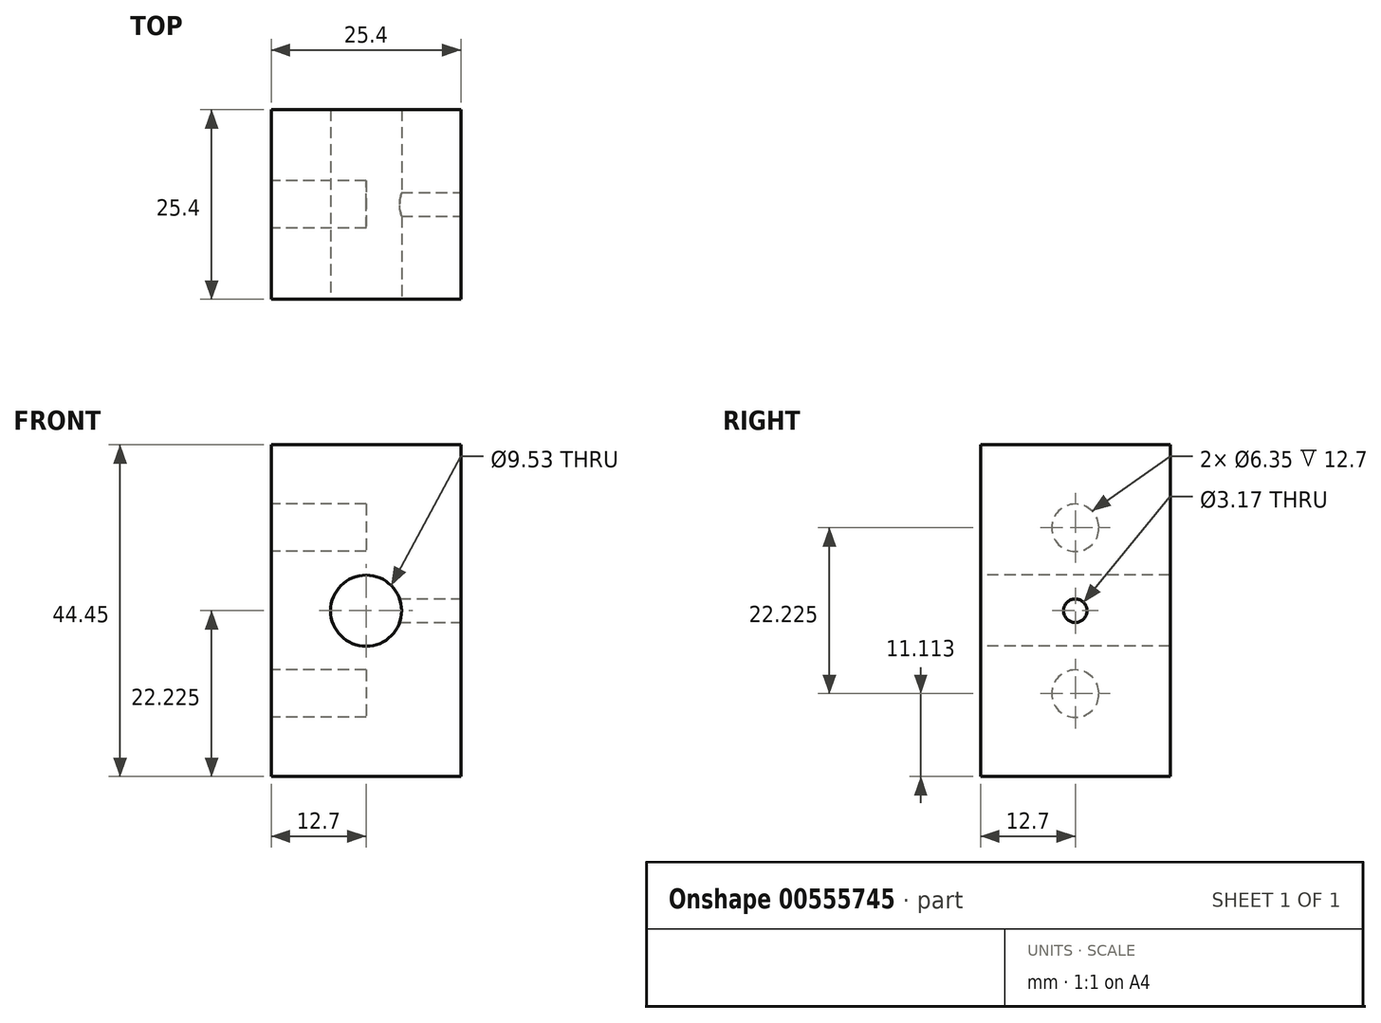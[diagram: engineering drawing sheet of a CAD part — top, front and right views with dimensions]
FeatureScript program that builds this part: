
annotation { "Feature Type Name" : "Feature", "Feature Type Description" : "" }
export const myFeature = defineFeature(function(context is Context, id is Id, definition is map)
    precondition{}
    {
        {
            var Q0;
            Q0=qCreatedBy(makeId("Top.planeOp"),FACE);
            var sketch = newSketch(context, id + "F0", { "sketchPlane" : qUnion([Q0])});
            skLineSegment(sketch, "E0.bottom", {"start": v(12.7, -12.7) * mm, "end": v(-12.7, -12.7) * mm});
            skLineSegment(sketch, "E0.top", {"start": v(12.7, 12.7) * mm, "end": v(-12.7, 12.7) * mm});
            skLineSegment(sketch, "E0.left", {"start": v(12.7, -12.7) * mm, "end": v(12.7, 12.7) * mm});
            skLineSegment(sketch, "E0.right", {"start": v(-12.7, -12.7) * mm, "end": v(-12.7, 12.7) * mm});
            skPoint(sketch, "E0.middle", {"position": v(0, 0) * mm});
            skSolve(sketch);
        }
        {
            var Q0;
            Q0 = qSketchRegion(id + "F0", true);
            extrude(context, id + "F1", {"entities" : qUnion([Q0]), "depth" : 44.45 * mm, "offsetDistance" : 25.4 * mm});
        }
        {
            var Q0;
            Q0=makeQuery(id+"F1.opExtrude","SWEPT_FACE",FACE,{"disambiguationData":[OSD([sQuery(id+"F0.wireOp",EDGE,"E0.bottom")])]});
            var sketch = newSketch(context, id + "F2", { "sketchPlane" : qUnion([Q0])});
            skCircle(sketch, "E1", {"center": v(0, 22.23) * mm, "radius": 4.76 * mm});
            skSolve(sketch);
        }
        {
            var Q0;
            Q0=makeQuery(id+"F2.imprint","IMPRINT",FACE,{"disambiguationData":[TD([[makeQuery(id+"F2.imprint","IMPRINT",EDGE,{"derivedFrom":sQuery(id+"F2.wireOp",EDGE,"E1")}),1.0]])]});
            extrude(context, id + "F3", {"entities" : qUnion([Q0]), "operationType" : NewBodyOperationType.REMOVE, "endBound" : BoundingType.THROUGH_ALL, "oppositeDirection" : true, "depth" : 25.4 * mm, "offsetDistance" : 25.4 * mm});
        }
        {
            var Q0;
            Q0=makeQuery(id+"F1.opExtrude","SWEPT_FACE",FACE,{"disambiguationData":[OSD([sQuery(id+"F0.wireOp",EDGE,"E0.left")])]});
            var sketch = newSketch(context, id + "F4", { "sketchPlane" : qUnion([Q0])});
            skCircle(sketch, "E2", {"center": v(0, 22.23) * mm, "radius": 1.59 * mm});
            skPoint(sketch, "E2.centerSnap0", {"position": v(12.7, 22.23) * mm});
            skSolve(sketch);
        }
        {
            var Q0;
            Q0 = qSketchRegion(id + "F4", true);
            extrude(context, id + "F5", {"entities" : qUnion([Q0]), "operationType" : NewBodyOperationType.REMOVE, "oppositeDirection" : true, "depth" : 12.7 * mm, "offsetDistance" : 25.4 * mm});
        }
        {
            var Q0;
            Q0=makeQuery(id+"F1.opExtrude","SWEPT_FACE",FACE,{"disambiguationData":[OSD([sQuery(id+"F0.wireOp",EDGE,"E0.right")])]});
            var sketch = newSketch(context, id + "F6", { "sketchPlane" : qUnion([Q0])});
            skCircle(sketch, "E3", {"center": v(0, 33.34) * mm, "radius": 3.18 * mm});
            skCircle(sketch, "E4", {"center": v(0, 11.11) * mm, "radius": 3.18 * mm});
            skSolve(sketch);
        }
        {
            var Q0;
            Q0=makeQuery(id+"F6.imprint","IMPRINT",FACE,{"disambiguationData":[TD([[makeQuery(id+"F6.imprint","IMPRINT",EDGE,{"derivedFrom":sQuery(id+"F6.wireOp",EDGE,"E3")}),1.0]])]});
            var Q1;
            Q1=makeQuery(id+"F6.imprint","IMPRINT",FACE,{"disambiguationData":[TD([[makeQuery(id+"F6.imprint","IMPRINT",EDGE,{"derivedFrom":sQuery(id+"F6.wireOp",EDGE,"E4")}),1.0]])]});
            extrude(context, id + "F7", {"entities" : qUnion([Q0, Q1]), "operationType" : NewBodyOperationType.REMOVE, "oppositeDirection" : true, "depth" : 12.7 * mm, "offsetDistance" : 25.4 * mm});
        }
    });
